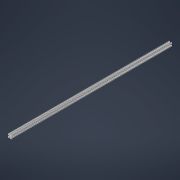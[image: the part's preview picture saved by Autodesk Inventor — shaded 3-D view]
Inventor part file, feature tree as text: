
AUTODESK INVENTOR PART (.ipt)
format: ipt  version: 2021 (Build 250183000, 183)  size: 345,600 bytes
history: native  units: mm
features: extrude x1, pattern_circular x1, chamfer x1, fillet x1, sketch x1, other x1
ambient origin geometry x8: Origin, YZ Plane, XZ Plane, XY Plane, X Axis, Y Axis, Z Axis, Center Point
bodies: Solid1 (feature_tree)
feature tree (6):
  extrude  "Extrusion1"  TaperAngle=135.0deg  [1 undecoded]
  pattern_circular  "Circular Pattern1"  Count=2  [1 undecoded]
  chamfer  "Chamfer1"  Distance=1000.0mm
  fillet  "Fillet1"  Radius=40.0mm
  sketch  "Sketch1"  dims[d0=1.5mm d6=6.3mm d9=4.6mm d18=135.0deg d22=20.0mm d24=1000.0mm d25=0.0mm d26=40.0mm d27=360.0deg d34=11.0mm d35=6.79mm d36=1.8mm d37=1.185mm d38=2.0mm d39=45.0deg d40=1.5mm]
  other  "Image1"
note: 2 required parameter values undecoded (feature->parameter linkage not recoverable at this tier; creation-order binding heuristic only, values carry confidence <= 0.55)
